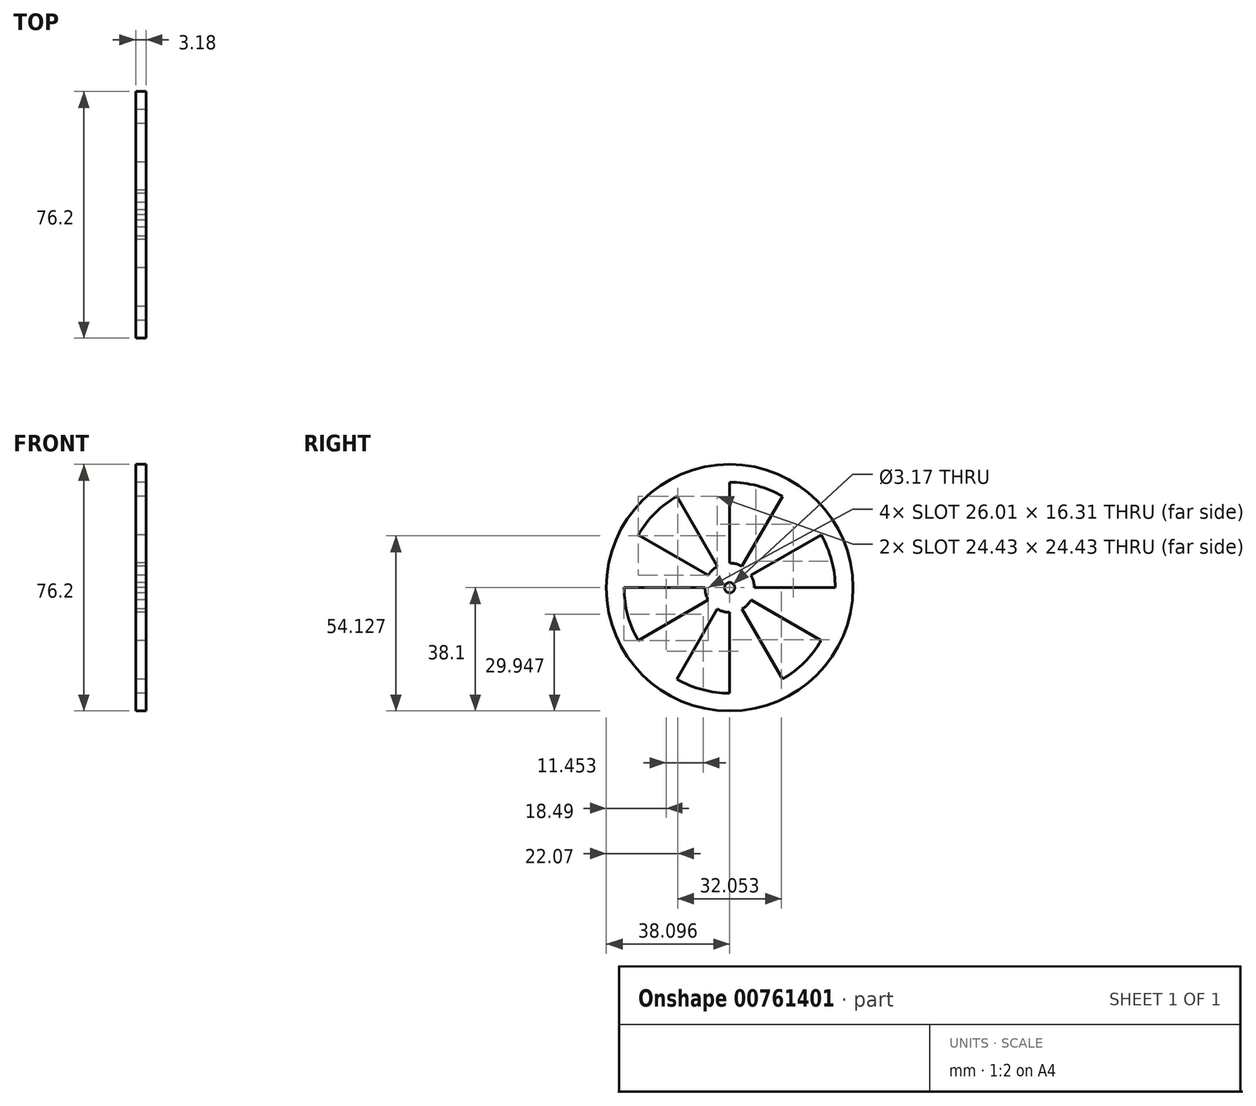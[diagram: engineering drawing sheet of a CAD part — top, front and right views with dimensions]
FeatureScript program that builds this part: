
annotation { "Feature Type Name" : "Feature", "Feature Type Description" : "" }
export const myFeature = defineFeature(function(context is Context, id is Id, definition is map)
    precondition{}
    {
        {
            var Q0;
            Q0=qCreatedBy(makeId("Right.planeOp"),FACE);
            var sketch = newSketch(context, id + "F0", { "sketchPlane" : qUnion([Q0])});
            skCircle(sketch, "E0", {"center": v(47.97, 0) * mm, "radius": 38.1 * mm});
            skArc(sketch, "E1", {"start": v(31.66, 28.24) * mm, "mid": v(24.9, 23.06) * mm, "end": v(19.72, 16.3) * mm});
            skArc(sketch, "E2", {"start": v(44.16, 6.6) * mm, "mid": v(42.58, 5.39) * mm, "end": v(41.37, 3.8) * mm});
            skLineSegment(sketch, "E3", {"start": v(47.97, -32.61) * mm, "end": v(47.97, 32.61) * mm});
            skLineSegment(sketch, "E4", {"start": v(15.35, 0) * mm, "end": v(80.58, 0) * mm});
            skLineSegment(sketch, "E5", {"start": v(47.97, 0) * mm, "end": v(31.66, 28.24) * mm});
            skLineSegment(sketch, "E6", {"start": v(47.97, 0) * mm, "end": v(19.72, 16.3) * mm});
            skLineSegment(sketch, "E7.MirrorCS", {"start": v(47.97, 32.61) * mm, "end": v(47.97, -32.61) * mm});
            skLineSegment(sketch, "E8.MirrorCS", {"start": v(47.97, 0) * mm, "end": v(31.66, -28.24) * mm});
            skLineSegment(sketch, "E9.MirrorCS", {"start": v(47.97, 0) * mm, "end": v(19.72, -16.3) * mm});
            skLineSegment(sketch, "E10.MirrorCS", {"start": v(47.97, 0) * mm, "end": v(64.27, 28.24) * mm});
            skLineSegment(sketch, "E11.MirrorCS", {"start": v(47.97, 0) * mm, "end": v(76.2, 16.3) * mm});
            skLineSegment(sketch, "E12.MirrorCS", {"start": v(47.97, 0) * mm, "end": v(76.2, -16.3) * mm});
            skLineSegment(sketch, "E13.MirrorCS", {"start": v(47.97, 0) * mm, "end": v(64.27, -28.24) * mm});
            skArc(sketch, "E14.trimOffspring", {"start": v(15.35, 0) * mm, "mid": v(16.47, -8.44) * mm, "end": v(19.72, -16.3) * mm});
            skArc(sketch, "E15.trimOffspring", {"start": v(31.66, -28.24) * mm, "mid": v(39.53, -31.5) * mm, "end": v(47.97, -32.61) * mm});
            skArc(sketch, "E16.trimOffspring", {"start": v(64.27, -28.24) * mm, "mid": v(71.03, -23.06) * mm, "end": v(76.2, -16.3) * mm});
            skArc(sketch, "E17.trimOffspring", {"start": v(80.58, 0) * mm, "mid": v(79.47, 8.44) * mm, "end": v(76.2, 16.3) * mm});
            skArc(sketch, "E18.trimOffspring", {"start": v(64.27, 28.24) * mm, "mid": v(56.4, 31.5) * mm, "end": v(47.97, 32.61) * mm});
            skArc(sketch, "E19.trimOffspring", {"start": v(51.78, 6.6) * mm, "mid": v(49.94, 7.36) * mm, "end": v(47.97, 7.62) * mm});
            skArc(sketch, "E20.trimOffspring", {"start": v(55.59, 0) * mm, "mid": v(55.33, 1.97) * mm, "end": v(54.57, 3.8) * mm});
            skArc(sketch, "E21.trimOffspring", {"start": v(51.78, -6.6) * mm, "mid": v(53.35, -5.39) * mm, "end": v(54.57, -3.8) * mm});
            skArc(sketch, "E22.trimOffspring", {"start": v(44.16, -6.6) * mm, "mid": v(46, -7.36) * mm, "end": v(47.97, -7.62) * mm});
            skArc(sketch, "E23.trimOffspring", {"start": v(40.35, 0) * mm, "mid": v(40.6, -1.97) * mm, "end": v(41.37, -3.8) * mm});
            skCircle(sketch, "E24", {"center": v(47.97, 0) * mm, "radius": 1.59 * mm});
            skSolve(sketch);
        }
        {
            var Q0;
            {var subQ3=sQuery(id+"F0.wireOp",EDGE,"E21.trimOffspring");Q0=makeQuery(id+"F0.imprint","IMPRINT",FACE,{"disambiguationData":[TD([[makeQuery(id+"F0.imprint","IMPRINT",EDGE,{"derivedFrom":subQ3}),1.0]])]});}
            var Q1;
            {var subQ3=sQuery(id+"F0.wireOp",EDGE,"E22.trimOffspring");Q1=makeQuery(id+"F0.imprint","IMPRINT",FACE,{"disambiguationData":[TD([[makeQuery(id+"F0.imprint","IMPRINT",EDGE,{"derivedFrom":subQ3}),1.0]])]});}
            var Q2;
            {var subQ3=sQuery(id+"F0.wireOp",EDGE,"E23.trimOffspring");Q2=makeQuery(id+"F0.imprint","IMPRINT",FACE,{"disambiguationData":[TD([[makeQuery(id+"F0.imprint","IMPRINT",EDGE,{"derivedFrom":subQ3}),1.0]])]});}
            var Q3;
            {var subQ0=sQuery(id+"F0.wireOp",EDGE,"E2");Q3=makeQuery(id+"F0.imprint","IMPRINT",FACE,{"disambiguationData":[TD([[makeQuery(id+"F0.imprint","IMPRINT",EDGE,{"derivedFrom":subQ0}),1.0]])]});}
            var Q4;
            {var subQ3=sQuery(id+"F0.wireOp",EDGE,"E19.trimOffspring");Q4=makeQuery(id+"F0.imprint","IMPRINT",FACE,{"disambiguationData":[TD([[makeQuery(id+"F0.imprint","IMPRINT",EDGE,{"derivedFrom":subQ3}),1.0]])]});}
            var Q5;
            {var subQ3=sQuery(id+"F0.wireOp",EDGE,"E20.trimOffspring");Q5=makeQuery(id+"F0.imprint","IMPRINT",FACE,{"disambiguationData":[TD([[makeQuery(id+"F0.imprint","IMPRINT",EDGE,{"derivedFrom":subQ3}),1.0]])]});}
            var Q6;
            Q6=makeQuery(id+"F0.imprint","IMPRINT",FACE,{"disambiguationData":[TD([[makeQuery(id+"F0.imprint","IMPRINT",EDGE,{"derivedFrom":sQuery(id+"F0.wireOp",EDGE,"E0")}),1.0]])]});
            extrude(context, id + "F1", {"entities" : qUnion([Q0, Q1, Q2, Q3, Q4, Q5, Q6]), "depth" : 3.17 * mm, "offsetDistance" : 25.4 * mm});
        }
    });
